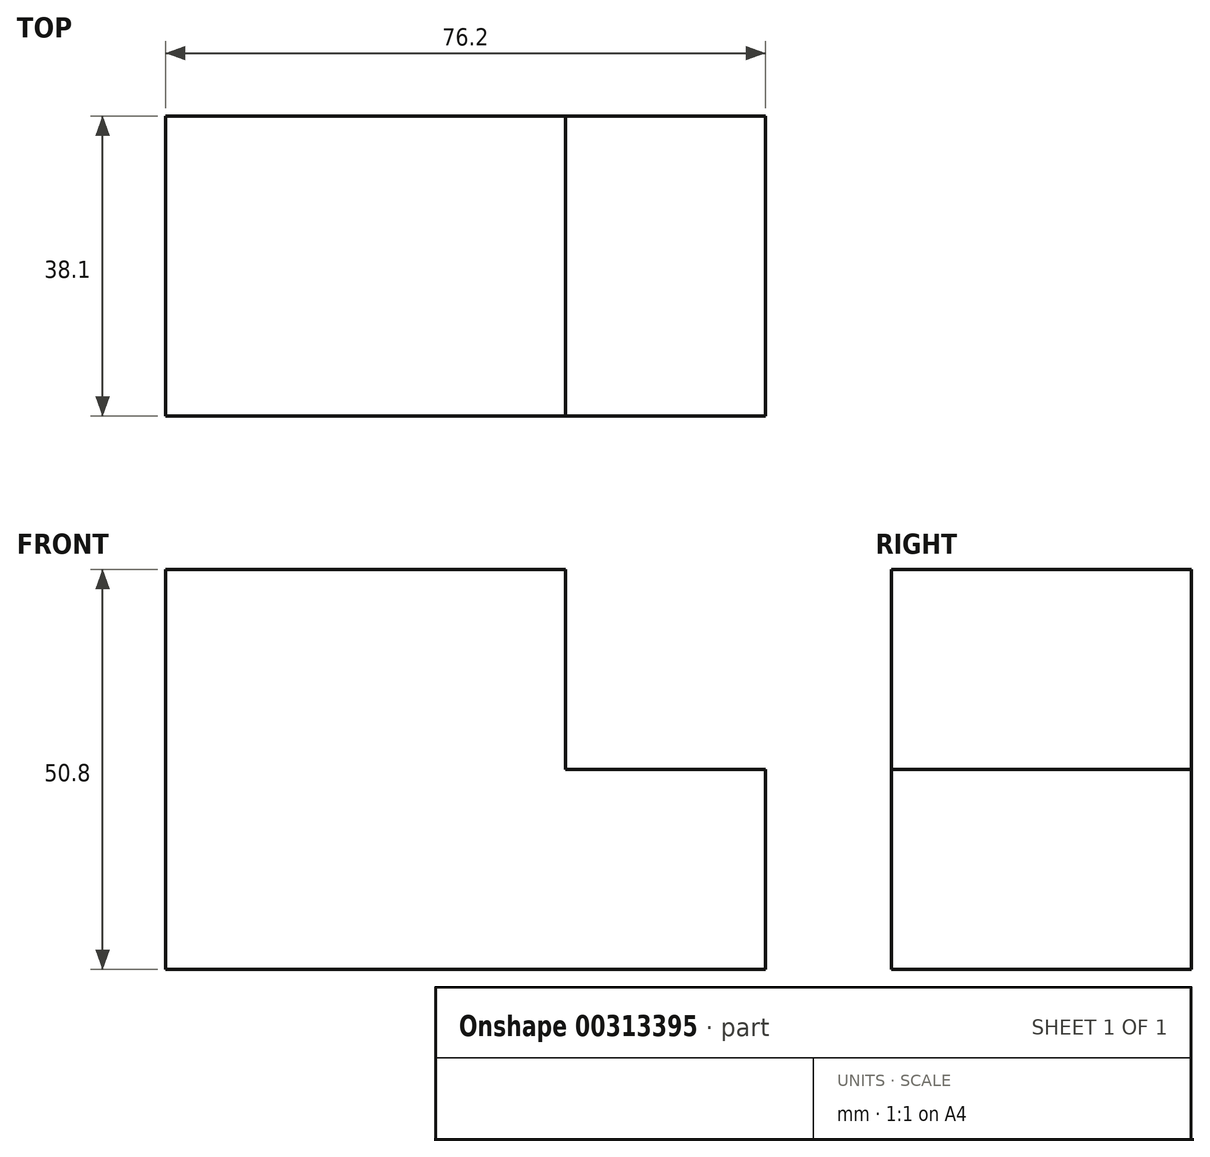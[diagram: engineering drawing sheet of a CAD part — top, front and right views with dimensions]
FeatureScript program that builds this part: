
annotation { "Feature Type Name" : "Feature", "Feature Type Description" : "" }
export const myFeature = defineFeature(function(context is Context, id is Id, definition is map)
    precondition{}
    {
        {
            var Q0;
            Q0=qCreatedBy(makeId("Front.planeOp"),FACE);
            var sketch = newSketch(context, id + "F0", { "sketchPlane" : qUnion([Q0])});
            skLineSegment(sketch, "E0", {"start": v(-17, -34.55) * mm, "end": v(59.2, -34.55) * mm});
            skLineSegment(sketch, "E1", {"start": v(59.2, -34.55) * mm, "end": v(59.2, -9.15) * mm});
            skLineSegment(sketch, "E2", {"start": v(59.2, -9.15) * mm, "end": v(33.8, -9.15) * mm});
            skLineSegment(sketch, "E3", {"start": v(33.8, -9.15) * mm, "end": v(33.8, 16.25) * mm});
            skLineSegment(sketch, "E4", {"start": v(33.8, 16.25) * mm, "end": v(-17, 16.25) * mm});
            skLineSegment(sketch, "E5", {"start": v(-17, 16.25) * mm, "end": v(-17, -34.55) * mm});
            skSolve(sketch);
        }
        {
            var Q0;
            Q0=makeQuery(id+"F0.imprint","IMPRINT",FACE,{"disambiguationData":[TD([[makeQuery(id+"F0.imprint","IMPRINT",EDGE,{"derivedFrom":sQuery(id+"F0.wireOp",EDGE,"E0")}),1.0]])]});
            extrude(context, id + "F1", {"entities" : qUnion([Q0]), "depth" : 38.1 * mm});
        }
    });
